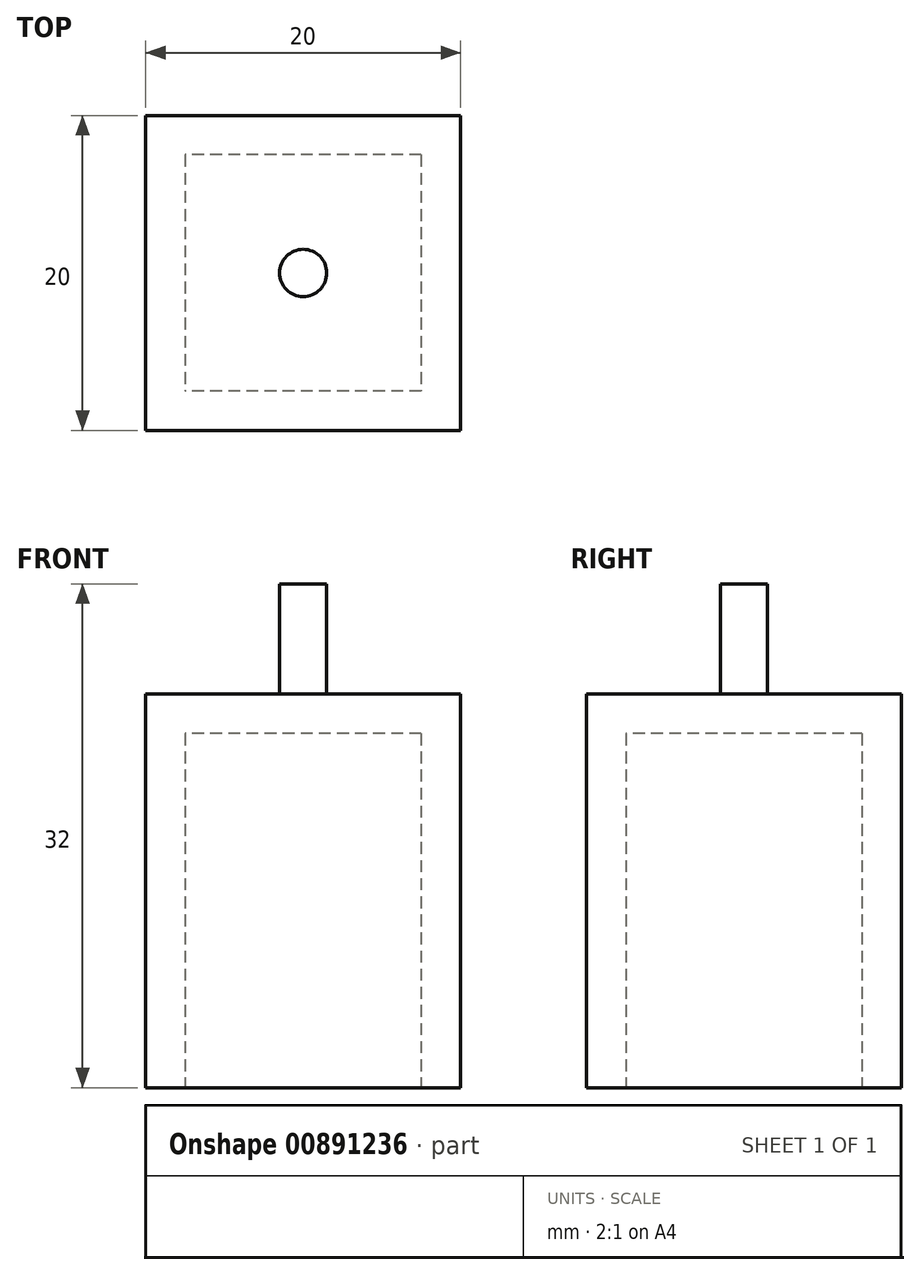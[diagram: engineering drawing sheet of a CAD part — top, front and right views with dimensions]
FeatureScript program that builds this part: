
annotation { "Feature Type Name" : "Feature", "Feature Type Description" : "" }
export const myFeature = defineFeature(function(context is Context, id is Id, definition is map)
    precondition{}
    {
        {
            var Q0;
            Q0=qCreatedBy(makeId("Top.planeOp"),FACE);
            var sketch = newSketch(context, id + "F0", { "sketchPlane" : qUnion([Q0])});
            skLineSegment(sketch, "E0.bottom", {"start": v(10, 10) * mm, "end": v(-10, 10) * mm});
            skLineSegment(sketch, "E0.top", {"start": v(10, -10) * mm, "end": v(-10, -10) * mm});
            skLineSegment(sketch, "E0.left", {"start": v(10, 10) * mm, "end": v(10, -10) * mm});
            skLineSegment(sketch, "E0.right", {"start": v(-10, 10) * mm, "end": v(-10, -10) * mm});
            skPoint(sketch, "E0.middle", {"position": v(0, 0) * mm});
            skSolve(sketch);
        }
        {
            var Q0;
            Q0 = qSketchRegion(id + "F0", true);
            extrude(context, id + "F1", {"entities" : qUnion([Q0]), "depth" : 25 * mm, "offsetDistance" : 25 * mm});
        }
        {
            var Q0;
            Q0=makeQuery(id+"F1.opExtrude","CAP_FACE",FACE,{"disambiguationData":[OSD([sQuery(id+"F0.wireOp",EDGE,"E0.bottom"),sQuery(id+"F0.wireOp",EDGE,"E0.top"),sQuery(id+"F0.wireOp",EDGE,"E0.left"),sQuery(id+"F0.wireOp",EDGE,"E0.right")])],"isStart":false});
            var sketch = newSketch(context, id + "F2", { "sketchPlane" : qUnion([Q0])});
            skCircle(sketch, "E1", {"center": v(0, 0) * mm, "radius": 1.5 * mm});
            skSolve(sketch);
        }
        {
            var Q0;
            Q0 = qSketchRegion(id + "F2", true);
            extrude(context, id + "F3", {"entities" : qUnion([Q0]), "operationType" : NewBodyOperationType.ADD, "depth" : 7 * mm, "offsetDistance" : 25 * mm});
        }
        {
            var Q0;
            Q0=makeQuery(id+"F1.opExtrude","CAP_FACE",FACE,{"disambiguationData":[OSD([sQuery(id+"F0.wireOp",EDGE,"E0.bottom"),sQuery(id+"F0.wireOp",EDGE,"E0.top"),sQuery(id+"F0.wireOp",EDGE,"E0.left"),sQuery(id+"F0.wireOp",EDGE,"E0.right")])],"isStart":true});
            shell(context, id + "F4", {"entities" : qUnion([Q0]), "thickness" : 2.5 * mm});
        }
    });
